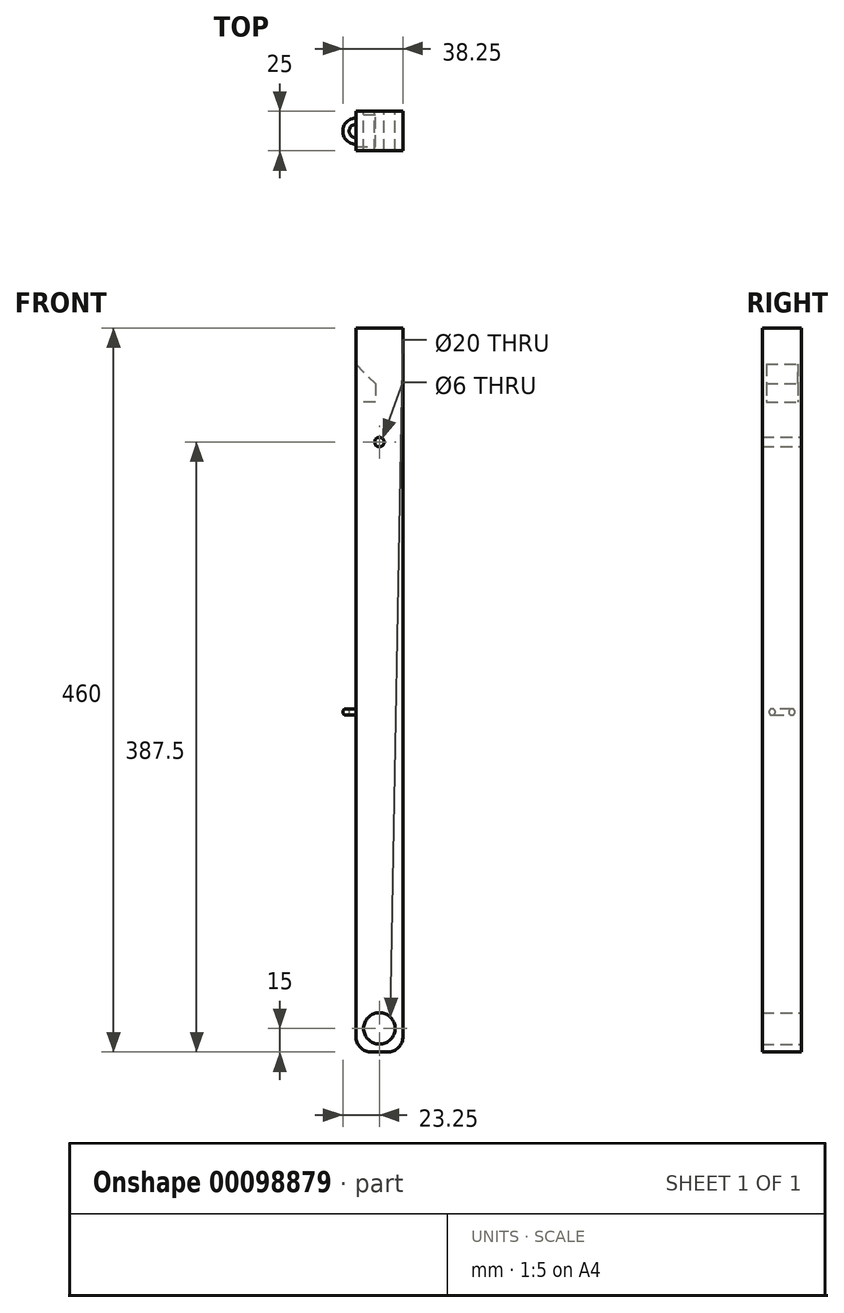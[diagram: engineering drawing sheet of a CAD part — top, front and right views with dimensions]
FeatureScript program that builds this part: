
annotation { "Feature Type Name" : "Feature", "Feature Type Description" : "" }
export const myFeature = defineFeature(function(context is Context, id is Id, definition is map)
    precondition{}
    {
        {
            var Q0;
            Q0=qCreatedBy(makeId("Front.planeOp"),FACE);
            var sketch = newSketch(context, id + "F0", { "sketchPlane" : qUnion([Q0])});
            skLineSegment(sketch, "E0.top", {"start": v(-5, -15) * mm, "end": v(5, -15) * mm});
            skLineSegment(sketch, "E0.left", {"start": v(-15, 15) * mm, "end": v(-15, -5) * mm});
            skLineSegment(sketch, "E0.right", {"start": v(15, 15) * mm, "end": v(15, -5) * mm});
            skPoint(sketch, "E0.middle", {"position": v(0, 0) * mm});
            skPoint(sketch, "E1.visualSharp", {"position": v(15, -15) * mm});
            skArc(sketch, "E1.filletArc", {"start": v(5, -15) * mm, "mid": v(12.07, -12.07) * mm, "end": v(15, -5) * mm});
            skPoint(sketch, "E2.visualSharp", {"position": v(-15, -15) * mm});
            skArc(sketch, "E2.filletArc", {"start": v(-15, -5) * mm, "mid": v(-12.07, -12.07) * mm, "end": v(-5, -15) * mm});
            skPoint(sketch, "E3.endSnap0", {"position": v(0, 15) * mm});
            skLineSegment(sketch, "E4.top", {"start": v(15, 445) * mm, "end": v(-15, 445) * mm});
            skLineSegment(sketch, "E4.left", {"start": v(15, 15) * mm, "end": v(15, 445) * mm});
            skLineSegment(sketch, "E4.right", {"start": v(-15, 15) * mm, "end": v(-15, 445) * mm});
            skPoint(sketch, "E4.middle", {"position": v(0, 230) * mm});
            skCircle(sketch, "E5", {"center": v(0, 0) * mm, "radius": 10 * mm});
            skSolve(sketch);
        }
        {
            var Q0;
            Q0 = qSketchRegion(id + "F0", true);
            extrude(context, id + "F1", {"entities" : qUnion([Q0]), "depth" : 25 * mm});
        }
        {
            var Q0;
            Q0=makeQuery(id+"F1.opExtrude","SWEPT_FACE",FACE,{"disambiguationData":[OSD([sQuery(id+"F0.wireOp",EDGE,"E0.left"),sQuery(id+"F0.wireOp",EDGE,"E4.right")])]});
            var sketch = newSketch(context, id + "F2", { "sketchPlane" : qUnion([Q0])});
            skLineSegment(sketch, "E6.bottom", {"start": v(22.5, 422) * mm, "end": v(2.5, 422) * mm});
            skLineSegment(sketch, "E6.top", {"start": v(22.5, 398) * mm, "end": v(2.5, 398) * mm});
            skLineSegment(sketch, "E6.left", {"start": v(22.5, 422) * mm, "end": v(22.5, 398) * mm});
            skLineSegment(sketch, "E6.right", {"start": v(2.5, 422) * mm, "end": v(2.5, 398) * mm});
            skPoint(sketch, "E6.middle", {"position": v(12.5, 410) * mm});
            skPoint(sketch, "E7.left.start.orphan", {"position": v(0, 425) * mm});
            skPoint(sketch, "E8.start.orphan", {"position": v(25, 425) * mm});
            skPoint(sketch, "E9.trimOffspring.end.orphan", {"position": v(0, 395) * mm});
            skPoint(sketch, "E10.end.orphan", {"position": v(12.5, 425) * mm});
            skPoint(sketch, "E10.start.orphan", {"position": v(12.5, 445) * mm});
            skSolve(sketch);
        }
        {
            var Q0;
            Q0=makeQuery(id+"F2.imprint","IMPRINT",FACE,{"disambiguationData":[TD([[makeQuery(id+"F2.imprint","IMPRINT",EDGE,{"derivedFrom":sQuery(id+"F2.wireOp",EDGE,"E6.bottom")}),1.0]])]});
            extrude(context, id + "F3", {"entities" : qUnion([Q0]), "operationType" : NewBodyOperationType.REMOVE, "oppositeDirection" : true, "depth" : 12.5 * mm});
        }
        {
            var Q0;
            Q0=makeQuery(id+"F3.boolean.opBoolean","COPY",EDGE,{"derivedFrom":makeQuery(id+"F3.opExtrude","CAP_EDGE",EDGE,{"disambiguationData":[OSD([sQuery(id+"F2.wireOp",EDGE,"E6.bottom")])],"isStart":false})});
            chamfer(context, id + "F4", {"entities" : qUnion([Q0]), "width" : 12.5 * mm, "tangentPropagation" : true});
        }
        {
            var Q0;
            Q0=makeQuery(id+"F1.opExtrude","SWEPT_FACE",FACE,{"disambiguationData":[OSD([sQuery(id+"F0.wireOp",EDGE,"E0.left"),sQuery(id+"F0.wireOp",EDGE,"E4.right")])]});
            var sketch = newSketch(context, id + "F5", { "sketchPlane" : qUnion([Q0])});
            skCircle(sketch, "E11", {"center": v(18.75, 201) * mm, "radius": 2 * mm});
            skCircle(sketch, "E12", {"center": v(6.25, 201) * mm, "radius": 2 * mm});
            skSolve(sketch);
        }
        {
            var Q0;
            Q0=sQuery(id+"F5.wireOp",VERTEX,"E12.center");
            var Q1;
            Q1=qCreatedBy(makeId("Top.planeOp"),FACE);
            cPlane(context, id + "F6", {"entities" : qUnion([Q0, Q1]), "cplaneType" : CPlaneType.PLANE_POINT, "offset" : 150 * mm, "width" : 150 * mm, "height" : 150 * mm});
        }
        {
            var Q0;
            Q0=qCreatedBy(id+"F6.planeOp",FACE);
            var sketch = newSketch(context, id + "F7", { "sketchPlane" : qUnion([Q0])});
            skArc(sketch, "E13", {"start": v(-15, -18.75) * mm, "mid": v(-21.25, -12.5) * mm, "end": v(-15, -6.25) * mm});
            skSolve(sketch);
        }
        {
            var Q0;
            Q0=makeQuery(id+"F5.imprint","IMPRINT",FACE,{"disambiguationData":[TD([[makeQuery(id+"F5.imprint","IMPRINT",EDGE,{"derivedFrom":sQuery(id+"F5.wireOp",EDGE,"E12")}),1.0]])]});
            var Q1;
            Q1=sQuery(id+"F7.wireOp",EDGE,"E13");
            sweep(context, id + "F8", {"operationType" : NewBodyOperationType.ADD, "profiles" : qUnion([Q0]), "path" : qUnion([Q1])});
        }
        {
            var Q0;
            Q0=makeQuery(id+"F1.opExtrude","CAP_FACE",FACE,{"disambiguationData":[OSD([sQuery(id+"F0.wireOp",EDGE,"E0.top"),sQuery(id+"F0.wireOp",EDGE,"E0.left"),sQuery(id+"F0.wireOp",EDGE,"E0.right"),sQuery(id+"F0.wireOp",EDGE,"E1.filletArc"),sQuery(id+"F0.wireOp",EDGE,"E2.filletArc"),sQuery(id+"F0.wireOp",EDGE,"E4.top"),sQuery(id+"F0.wireOp",EDGE,"E4.left"),sQuery(id+"F0.wireOp",EDGE,"E4.right"),sQuery(id+"F0.wireOp",EDGE,"E5")])],"isStart":true});
            var sketch = newSketch(context, id + "F9", { "sketchPlane" : qUnion([Q0])});
            skCircle(sketch, "E14", {"center": v(0, 372.5) * mm, "radius": 3 * mm});
            skPoint(sketch, "E15.start.orphan", {"position": v(0, -15) * mm});
            skSolve(sketch);
        }
        {
            var Q0;
            Q0=makeQuery(id+"F9.imprint","IMPRINT",FACE,{"disambiguationData":[TD([[makeQuery(id+"F9.imprint","IMPRINT",EDGE,{"derivedFrom":sQuery(id+"F9.wireOp",EDGE,"E14")}),1.0]])]});
            extrude(context, id + "F10", {"entities" : qUnion([Q0]), "operationType" : NewBodyOperationType.REMOVE, "endBound" : BoundingType.UP_TO_NEXT, "oppositeDirection" : true, "depth" : 25 * mm});
        }
    });
